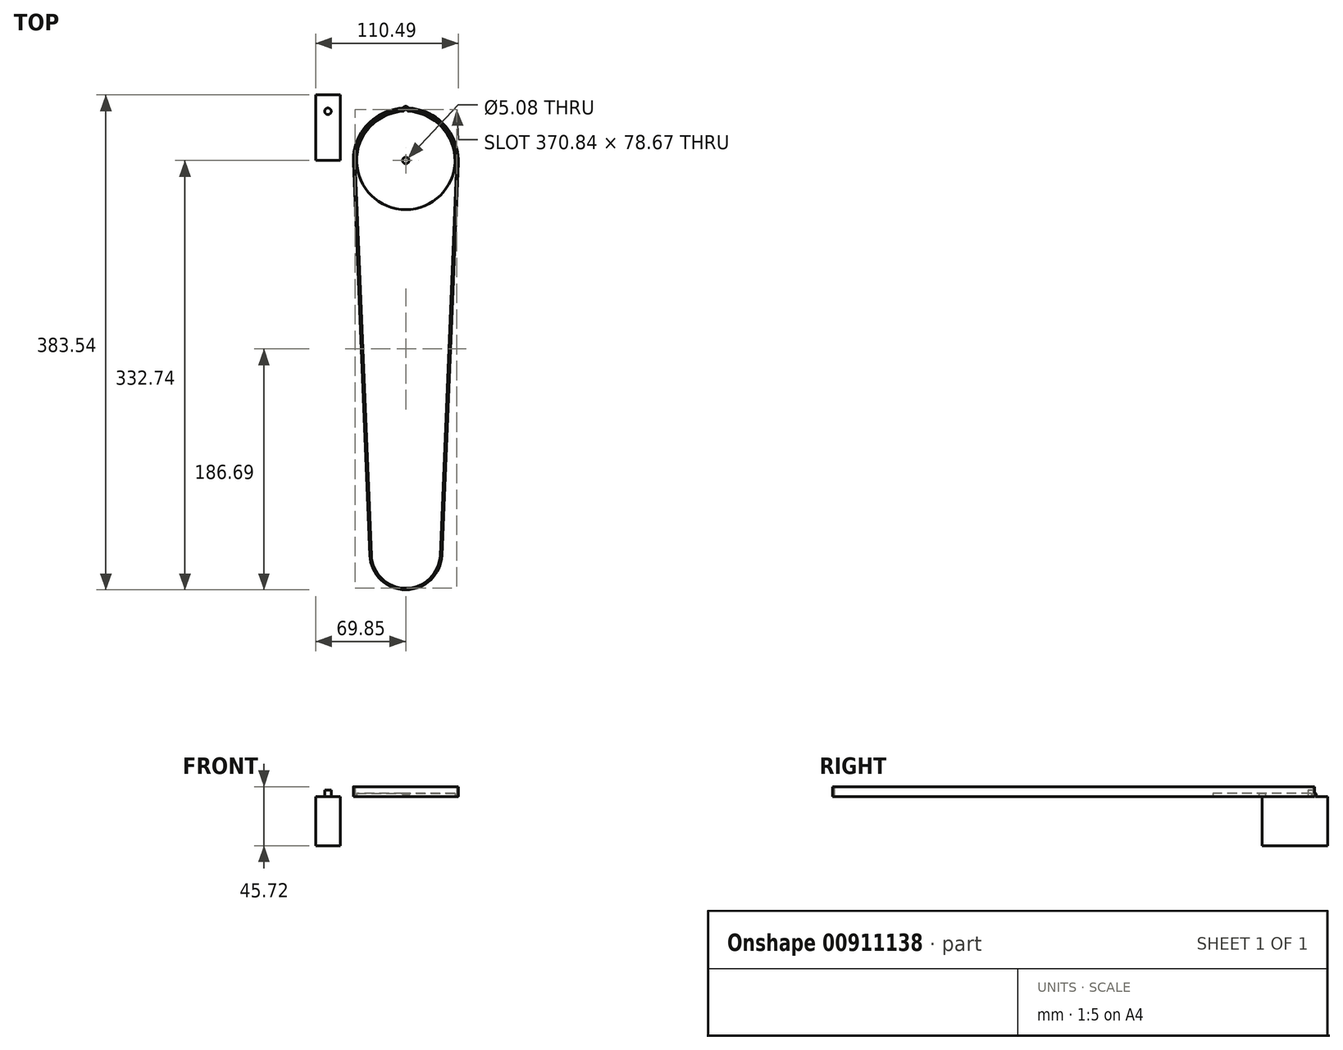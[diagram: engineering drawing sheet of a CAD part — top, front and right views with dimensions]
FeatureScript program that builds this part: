
annotation { "Feature Type Name" : "Feature", "Feature Type Description" : "" }
export const myFeature = defineFeature(function(context is Context, id is Id, definition is map)
    precondition{}
    {
        {
            var Q0;
            Q0=qCreatedBy(makeId("Top.planeOp"),FACE);
            var sketch = newSketch(context, id + "F0", { "sketchPlane" : qUnion([Q0])});
            skCircle(sketch, "E0", {"center": v(0, 0) * mm, "radius": 38.1 * mm});
            skCircle(sketch, "E1", {"center": v(0, 0) * mm, "radius": 2.54 * mm});
            skSolve(sketch);
        }
        {
            var Q0;
            Q0=makeQuery(id+"F0.imprint","IMPRINT",FACE,{"disambiguationData":[TD([[makeQuery(id+"F0.imprint","IMPRINT",EDGE,{"derivedFrom":sQuery(id+"F0.wireOp",EDGE,"E1")}),-1.0]])]});
            var Q1;
            {var subQ5=sQuery(id+"F0.wireOp",EDGE,"pq5Jjkm7-a4fV-90wC-CFVI-NsJcmO3FdSo2.bottom");Q1=makeQuery(id+"F0.imprint","IMPRINT",FACE,{"disambiguationData":[TD([[makeQuery(id+"F0.imprint","IMPRINT",EDGE,{"derivedFrom":subQ5}),1.0]])]});}
            extrude(context, id + "F1", {"entities" : qUnion([Q0, Q1]), "depth" : 2.54 * mm, "offsetDistance" : 25.4 * mm});
        }
        {
            var Q0;
            Q0=qCreatedBy(makeId("Top.planeOp"),FACE);
            var sketch = newSketch(context, id + "F2", { "sketchPlane" : qUnion([Q0])});
            skLineSegment(sketch, "E2.MirrorCS", {"start": v(1.27, 41.86) * mm, "end": v(0, 41.86) * mm});
            skLineSegment(sketch, "E3.MirrorCS", {"start": v(2.03, 38.05) * mm, "end": v(1.27, 41.86) * mm});
            skCircle(sketch, "E4.0", {"center": v(0, 0) * mm, "radius": 38.1 * mm});
            skLineSegment(sketch, "E5.MirrorCS", {"start": v(-1.27, 41.86) * mm, "end": v(0, 41.86) * mm});
            skLineSegment(sketch, "E6.MirrorCS", {"start": v(-2.03, 38.05) * mm, "end": v(-1.27, 41.86) * mm});
            skSolve(sketch);
        }
        {
            var Q0;
            Q0=qSketchRegion(id+"F2",true);
            var Q1;
            Q1=makeQuery(id+"F1.opExtrude","CAP_FACE",FACE,{"disambiguationData":[OSD([sQuery(id+"F0.wireOp",EDGE,"E0"),sQuery(id+"F0.wireOp",EDGE,"E1")])],"isStart":false});
            extrude(context, id + "F3", {"entities" : qUnion([Q0]), "operationType" : NewBodyOperationType.ADD, "endBound" : BoundingType.UP_TO_SURFACE, "depth" : 2.54 * mm, "endBoundEntityFace" : qUnion([Q1]), "offsetDistance" : 25.4 * mm});
        }
        {
            var Q0;
            Q0=makeQuery(id+"F3.opExtrude","CAP_EDGE",EDGE,{"disambiguationData":[OSD([sQuery(id+"F2.wireOp",EDGE,"E6.MirrorCS")])],"isStart":false});
            var Q1;
            Q1=makeQuery(id+"F3.opExtrude","CAP_EDGE",EDGE,{"disambiguationData":[OSD([sQuery(id+"F2.wireOp",EDGE,"E3.MirrorCS")])],"isStart":false});
            var Q2;
            Q2=makeQuery(id+"F3.opExtrude","CAP_EDGE",EDGE,{"disambiguationData":[OSD([sQuery(id+"F2.wireOp",EDGE,"E6.MirrorCS")])],"isStart":true});
            var Q3;
            Q3=makeQuery(id+"F3.opExtrude","CAP_EDGE",EDGE,{"disambiguationData":[OSD([sQuery(id+"F2.wireOp",EDGE,"E3.MirrorCS")])],"isStart":true});
            var Q4;
            Q4=makeQuery(id+"F3.opExtrude","SWEPT_EDGE",EDGE,{"disambiguationData":[OSD([sQuery(id+"F2.wireOp",EDGE,"E2.MirrorCS"),sQuery(id+"F2.wireOp",EDGE,"E3.MirrorCS")])]});
            var Q5;
            Q5=makeQuery(id+"F3.opExtrude","CAP_EDGE",EDGE,{"disambiguationData":[OSD([sQuery(id+"F2.wireOp",EDGE,"E2.MirrorCS"),sQuery(id+"F2.wireOp",EDGE,"E5.MirrorCS")])],"isStart":false});
            var Q6;
            Q6=makeQuery(id+"F3.opExtrude","SWEPT_EDGE",EDGE,{"disambiguationData":[OSD([sQuery(id+"F2.wireOp",EDGE,"E5.MirrorCS"),sQuery(id+"F2.wireOp",EDGE,"E6.MirrorCS")])]});
            var Q7;
            Q7=makeQuery(id+"F3.opExtrude","CAP_EDGE",EDGE,{"disambiguationData":[OSD([sQuery(id+"F2.wireOp",EDGE,"E2.MirrorCS"),sQuery(id+"F2.wireOp",EDGE,"E5.MirrorCS")])],"isStart":true});
            chamfer(context, id + "F4", {"entities" : qUnion([Q0, Q1, Q2, Q3, Q4, Q5, Q6, Q7]), "width" : 0.5 * mm, "tangentPropagation" : true});
        }
        {
            var Q0;
            Q0=makeQuery(id+"F0.imprint","IMPRINT",FACE,{"disambiguationData":[TD([[makeQuery(id+"F0.imprint","IMPRINT",EDGE,{"derivedFrom":sQuery(id+"F0.wireOp",EDGE,"E1")}),1.0]])]});
            extrude(context, id + "F5", {"entities" : qUnion([Q0]), "operationType" : NewBodyOperationType.REMOVE, "endBound" : BoundingType.THROUGH_ALL, "depth" : 25.4 * mm, "offsetDistance" : 25.4 * mm});
        }
        {
            var Q0;
            Q0=qCreatedBy(makeId("Top.planeOp"),FACE);
            var sketch = newSketch(context, id + "F6", { "sketchPlane" : qUnion([Q0])});
            skLineSegment(sketch, "E7.bottom", {"start": v(-69.85, 0) * mm, "end": v(-50.8, 0) * mm});
            skLineSegment(sketch, "E7.top", {"start": v(-69.85, 50.8) * mm, "end": v(-50.8, 50.8) * mm});
            skLineSegment(sketch, "E7.left", {"start": v(-69.85, 0) * mm, "end": v(-69.85, 50.8) * mm});
            skLineSegment(sketch, "E7.right", {"start": v(-50.8, 0) * mm, "end": v(-50.8, 50.8) * mm});
            skCircle(sketch, "E8", {"center": v(-60.33, 38.1) * mm, "radius": 2.54 * mm});
            skSolve(sketch);
        }
        {
            var Q0;
            Q0=makeQuery(id+"F6.imprint","IMPRINT",FACE,{"disambiguationData":[TD([[makeQuery(id+"F6.imprint","IMPRINT",EDGE,{"derivedFrom":sQuery(id+"F6.wireOp",EDGE,"E8")}),1.0]])]});
            var Q1;
            Q1=makeQuery(id+"F6.imprint","IMPRINT",FACE,{"disambiguationData":[TD([[makeQuery(id+"F6.imprint","IMPRINT",EDGE,{"derivedFrom":sQuery(id+"F6.wireOp",EDGE,"E7.bottom")}),1.0]])]});
            extrude(context, id + "F7", {"entities" : qUnion([Q0, Q1]), "oppositeDirection" : true, "depth" : 38.1 * mm, "offsetDistance" : 25.4 * mm});
        }
        {
            var Q0;
            Q0=makeQuery(id+"F6.imprint","IMPRINT",FACE,{"disambiguationData":[TD([[makeQuery(id+"F6.imprint","IMPRINT",EDGE,{"derivedFrom":sQuery(id+"F6.wireOp",EDGE,"E8")}),1.0]])]});
            extrude(context, id + "F8", {"entities" : qUnion([Q0]), "operationType" : NewBodyOperationType.ADD, "depth" : 5.08 * mm, "offsetDistance" : 25.4 * mm});
        }
        {
            var Q0;
            Q0=qCreatedBy(makeId("Top.planeOp"),FACE);
            var sketch = newSketch(context, id + "F9", { "sketchPlane" : qUnion([Q0])});
            skArc(sketch, "E9", {"start": v(39.34, -1.64) * mm, "mid": v(0, 39.37) * mm, "end": v(-39.34, -1.64) * mm});
            skArc(sketch, "E10", {"start": v(40.6, -1.7) * mm, "mid": v(0, 40.64) * mm, "end": v(-40.6, -1.7) * mm});
            skArc(sketch, "E11", {"start": v(-26.65, -305.91) * mm, "mid": v(0, -331.47) * mm, "end": v(26.65, -305.91) * mm});
            skArc(sketch, "E12", {"start": v(-27.92, -305.96) * mm, "mid": v(0, -332.74) * mm, "end": v(27.92, -305.96) * mm});
            skLineSegment(sketch, "E13", {"start": v(40.6, -1.7) * mm, "end": v(27.92, -305.96) * mm});
            skLineSegment(sketch, "E14", {"start": v(-40.6, -1.7) * mm, "end": v(-27.92, -305.96) * mm});
            skLineSegment(sketch, "E15", {"start": v(39.34, -1.64) * mm, "end": v(26.65, -305.91) * mm});
            skLineSegment(sketch, "E16", {"start": v(-39.34, -1.64) * mm, "end": v(-26.65, -305.91) * mm});
            skSolve(sketch);
        }
        {
            var Q0;
            Q0=makeQuery(id+"F9.imprint","IMPRINT",FACE,{"disambiguationData":[TD([[makeQuery(id+"F9.imprint","IMPRINT",EDGE,{"derivedFrom":sQuery(id+"F9.wireOp",EDGE,"E9")}),-1.0]])]});
            extrude(context, id + "F10", {"entities" : qUnion([Q0]), "depth" : 7.62 * mm, "offsetDistance" : 25.4 * mm});
        }
    });
